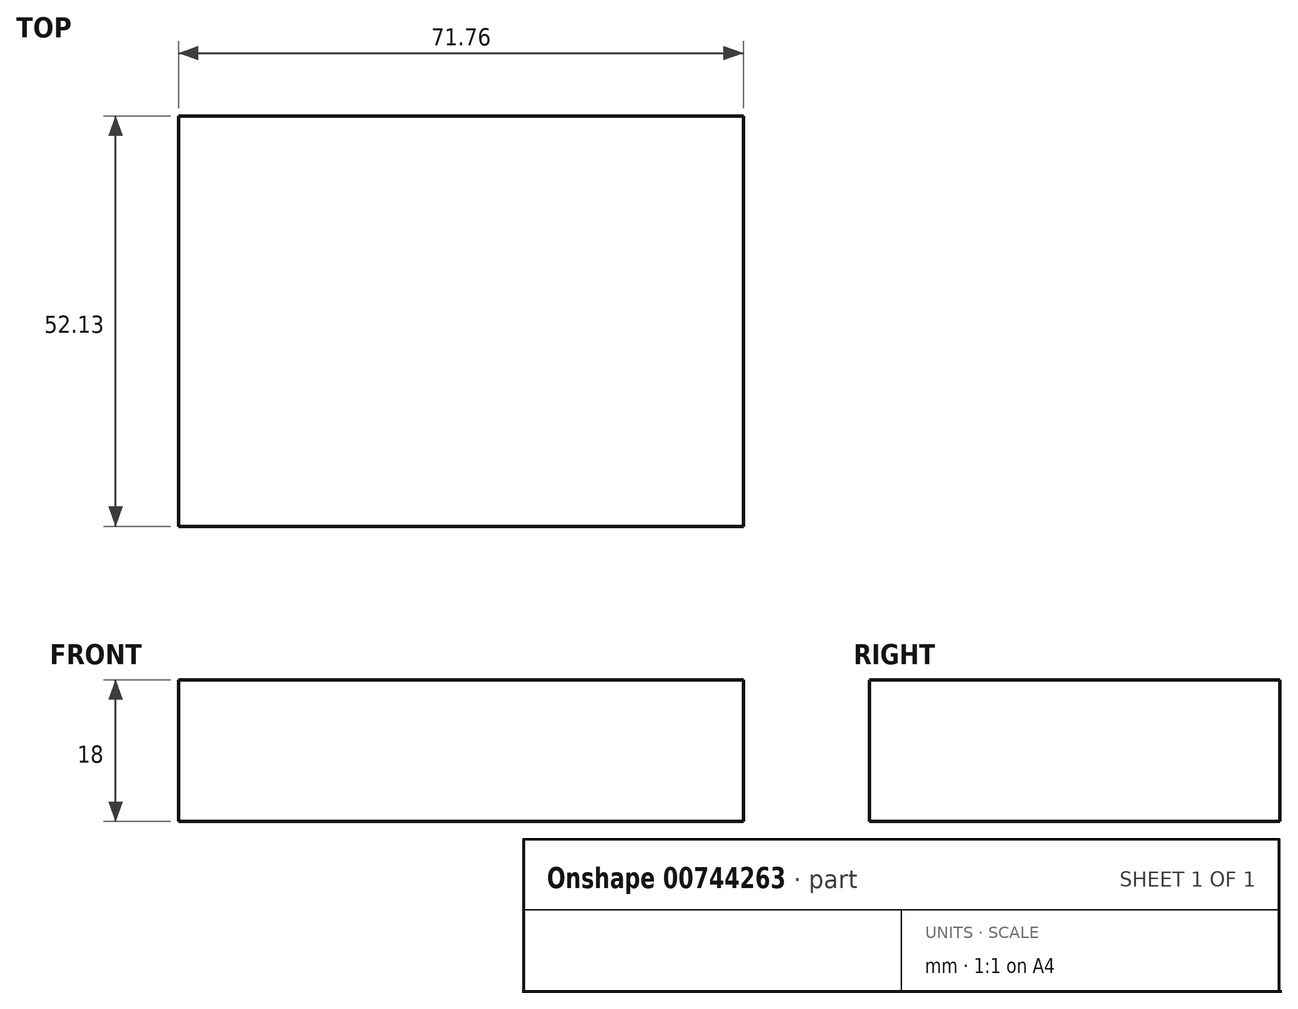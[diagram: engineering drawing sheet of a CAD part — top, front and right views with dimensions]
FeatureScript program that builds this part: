
annotation { "Feature Type Name" : "Feature", "Feature Type Description" : "" }
export const myFeature = defineFeature(function(context is Context, id is Id, definition is map)
    precondition{}
    {
        {
            var Q0;
            Q0=qCreatedBy(makeId("Top.planeOp"),FACE);
            var sketch = newSketch(context, id + "F0", { "sketchPlane" : qUnion([Q0])});
            skLineSegment(sketch, "E0.bottom", {"start": v(0, 0) * mm, "end": v(-71.76, 0) * mm});
            skLineSegment(sketch, "E0.top", {"start": v(0, 52.13) * mm, "end": v(-71.76, 52.13) * mm});
            skLineSegment(sketch, "E0.left", {"start": v(0, 0) * mm, "end": v(0, 52.13) * mm});
            skLineSegment(sketch, "E0.right", {"start": v(-71.76, 0) * mm, "end": v(-71.76, 52.13) * mm});
            skSolve(sketch);
        }
        {
            var Q0;
            Q0=makeQuery(id+"F0.imprint","IMPRINT",FACE,{"disambiguationData":[TD([[makeQuery(id+"F0.imprint","IMPRINT",EDGE,{"derivedFrom":sQuery(id+"F0.wireOp",EDGE,"E0.bottom")}),-1.0]])]});
            extrude(context, id + "F1", {"entities" : qUnion([Q0]), "depth" : 18 * mm, "offsetDistance" : 25.4 * mm});
        }
    });
